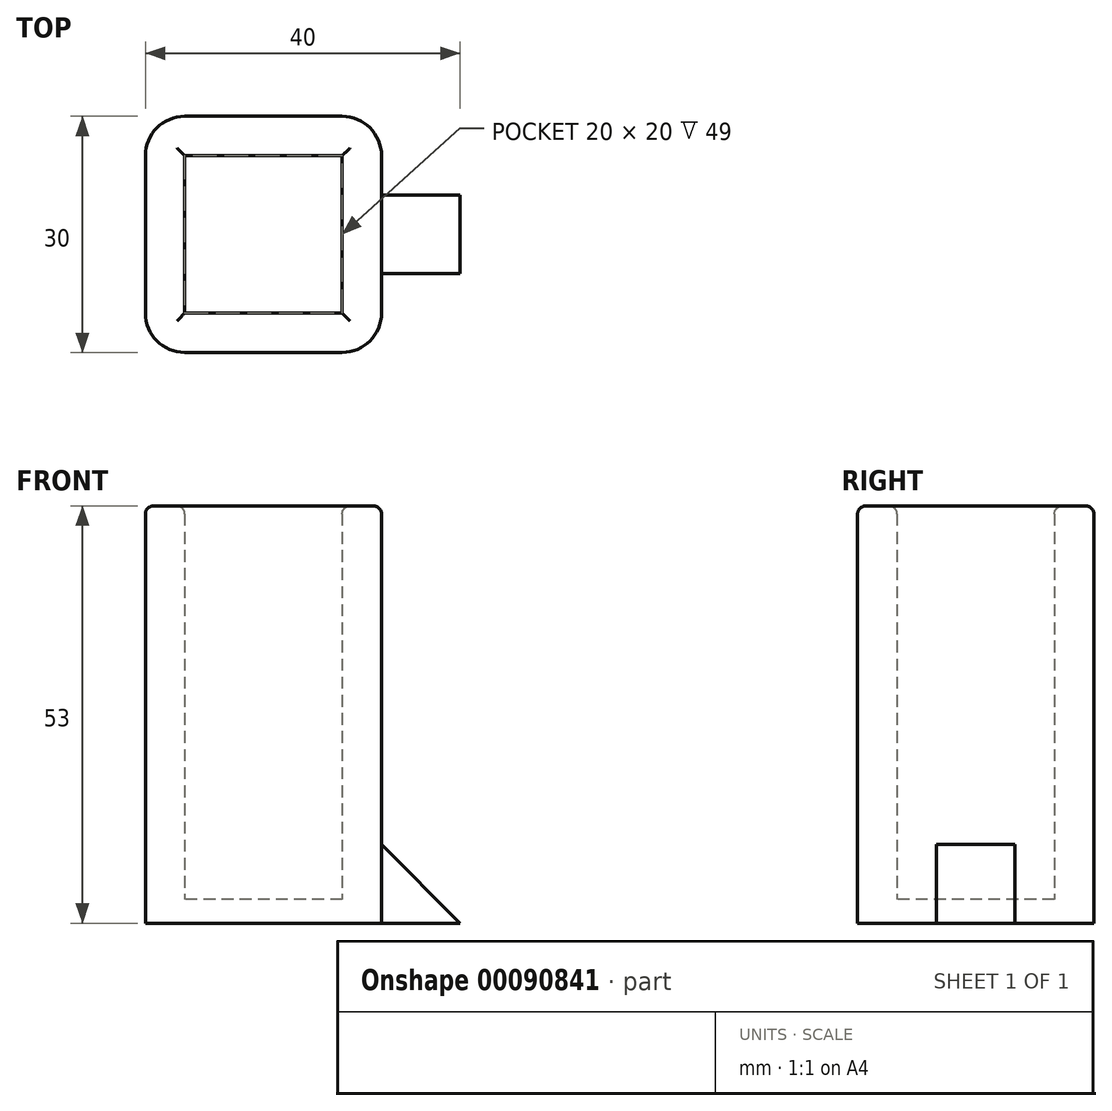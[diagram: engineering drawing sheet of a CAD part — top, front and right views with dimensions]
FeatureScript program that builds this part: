
annotation { "Feature Type Name" : "Feature", "Feature Type Description" : "" }
export const myFeature = defineFeature(function(context is Context, id is Id, definition is map)
    precondition{}
    {
        {
            var Q0;
            Q0=qCreatedBy(makeId("Top.planeOp"),FACE);
            var sketch = newSketch(context, id + "F0", { "sketchPlane" : qUnion([Q0])});
            skLineSegment(sketch, "E0.bottom", {"start": v(15, 15) * mm, "end": v(-15, 15) * mm});
            skLineSegment(sketch, "E0.top", {"start": v(15, -15) * mm, "end": v(-15, -15) * mm});
            skLineSegment(sketch, "E0.left", {"start": v(15, 15) * mm, "end": v(15, -15) * mm});
            skLineSegment(sketch, "E0.right", {"start": v(-15, 15) * mm, "end": v(-15, -15) * mm});
            skPoint(sketch, "E0.middle", {"position": v(0, 0) * mm});
            skSolve(sketch);
        }
        {
            var Q0;
            Q0 = qSketchRegion(id + "F0", true);
            extrude(context, id + "F1", {"entities" : qUnion([Q0]), "depth" : 3 * mm});
        }
        {
            var Q0;
            Q0=makeQuery(id+"F1.opExtrude","CAP_FACE",FACE,{"disambiguationData":[OSD([sQuery(id+"F0.wireOp",EDGE,"E0.bottom"),sQuery(id+"F0.wireOp",EDGE,"E0.top"),sQuery(id+"F0.wireOp",EDGE,"E0.left"),sQuery(id+"F0.wireOp",EDGE,"E0.right")])],"isStart":false});
            var sketch = newSketch(context, id + "F2", { "sketchPlane" : qUnion([Q0])});
            skLineSegment(sketch, "E1.bottom", {"start": v(15, 15) * mm, "end": v(-15, 15) * mm});
            skLineSegment(sketch, "E1.top", {"start": v(15, -15) * mm, "end": v(-15, -15) * mm});
            skLineSegment(sketch, "E1.left", {"start": v(15, 15) * mm, "end": v(15, -15) * mm});
            skLineSegment(sketch, "E1.right", {"start": v(-15, 15) * mm, "end": v(-15, -15) * mm});
            skPoint(sketch, "E1.middle", {"position": v(0, 0) * mm});
            skLineSegment(sketch, "E2.bottom", {"start": v(10, 10) * mm, "end": v(-10, 10) * mm});
            skLineSegment(sketch, "E2.top", {"start": v(10, -10) * mm, "end": v(-10, -10) * mm});
            skLineSegment(sketch, "E2.left", {"start": v(10, 10) * mm, "end": v(10, -10) * mm});
            skLineSegment(sketch, "E2.right", {"start": v(-10, 10) * mm, "end": v(-10, -10) * mm});
            skSolve(sketch);
        }
        {
            var Q0;
            Q0 = qSketchRegion(id + "F2", true);
            extrude(context, id + "F3", {"entities" : qUnion([Q0]), "operationType" : NewBodyOperationType.ADD, "depth" : 50 * mm});
        }
        {
            var Q0;
            Q0=makeQuery(id+"F3.boolean.opBoolean","MERGE",EDGE,{"derivedFrom":[makeQuery(id+"F1.opExtrude","SWEPT_EDGE",EDGE,{"disambiguationData":[OSD([sQuery(id+"F0.wireOp",EDGE,"E0.top"),sQuery(id+"F0.wireOp",EDGE,"E0.right")])]}),makeQuery(id+"F3.opExtrude","SWEPT_EDGE",EDGE,{"disambiguationData":[OSD([sQuery(id+"F2.wireOp",EDGE,"E1.top"),sQuery(id+"F2.wireOp",EDGE,"E1.right")])]})]});
            var Q1;
            Q1=makeQuery(id+"F3.boolean.opBoolean","MERGE",EDGE,{"derivedFrom":[makeQuery(id+"F1.opExtrude","SWEPT_EDGE",EDGE,{"disambiguationData":[OSD([sQuery(id+"F0.wireOp",EDGE,"E0.bottom"),sQuery(id+"F0.wireOp",EDGE,"E0.right")])]}),makeQuery(id+"F3.opExtrude","SWEPT_EDGE",EDGE,{"disambiguationData":[OSD([sQuery(id+"F2.wireOp",EDGE,"E1.bottom"),sQuery(id+"F2.wireOp",EDGE,"E1.right")])]})]});
            var Q2;
            Q2=makeQuery(id+"F3.boolean.opBoolean","MERGE",EDGE,{"derivedFrom":[makeQuery(id+"F1.opExtrude","SWEPT_EDGE",EDGE,{"disambiguationData":[OSD([sQuery(id+"F0.wireOp",EDGE,"E0.bottom"),sQuery(id+"F0.wireOp",EDGE,"E0.left")])]}),makeQuery(id+"F3.opExtrude","SWEPT_EDGE",EDGE,{"disambiguationData":[OSD([sQuery(id+"F2.wireOp",EDGE,"E1.bottom"),sQuery(id+"F2.wireOp",EDGE,"E1.left")])]})]});
            var Q3;
            Q3=makeQuery(id+"F3.boolean.opBoolean","MERGE",EDGE,{"derivedFrom":[makeQuery(id+"F1.opExtrude","SWEPT_EDGE",EDGE,{"disambiguationData":[OSD([sQuery(id+"F0.wireOp",EDGE,"E0.top"),sQuery(id+"F0.wireOp",EDGE,"E0.left")])]}),makeQuery(id+"F3.opExtrude","SWEPT_EDGE",EDGE,{"disambiguationData":[OSD([sQuery(id+"F2.wireOp",EDGE,"E1.top"),sQuery(id+"F2.wireOp",EDGE,"E1.left")])]})]});
            fillet(context, id + "F4", {"entities" : qUnion([Q0, Q1, Q2, Q3]), "radius" : 5 * mm, "tangentPropagation" : true, "allowEdgeOverflow" : false});
        }
        {
            var Q0;
            Q0=makeQuery(id+"F3.opExtrude","CAP_FACE",FACE,{"disambiguationData":[OSD([sQuery(id+"F2.wireOp",EDGE,"E1.bottom"),sQuery(id+"F2.wireOp",EDGE,"E1.top"),sQuery(id+"F2.wireOp",EDGE,"E1.left"),sQuery(id+"F2.wireOp",EDGE,"E1.right"),sQuery(id+"F2.wireOp",EDGE,"E2.bottom"),sQuery(id+"F2.wireOp",EDGE,"E2.top"),sQuery(id+"F2.wireOp",EDGE,"E2.left"),sQuery(id+"F2.wireOp",EDGE,"E2.right")])],"isStart":false});
            fillet(context, id + "F5", {"entities" : qUnion([Q0]), "radius" : 1 * mm, "tangentPropagation" : true, "allowEdgeOverflow" : false});
        }
        {
            var Q0;
            Q0=qCreatedBy(makeId("Front.planeOp"),FACE);
            var sketch = newSketch(context, id + "F6", { "sketchPlane" : qUnion([Q0])});
            skLineSegment(sketch, "E3", {"start": v(15, 0) * mm, "end": v(15, 10) * mm});
            skLineSegment(sketch, "E4", {"start": v(15, 10) * mm, "end": v(25, 0) * mm});
            skLineSegment(sketch, "E5", {"start": v(25, 0) * mm, "end": v(15, 0) * mm});
            skLineSegment(sketch, "E6", {"start": v(0, 0) * mm, "end": v(0, 15) * mm, "construction": true});
            skSolve(sketch);
        }
        {
            var Q0;
            Q0 = qSketchRegion(id + "F6", true);
            extrude(context, id + "F7", {"entities" : qUnion([Q0]), "operationType" : NewBodyOperationType.ADD, "depth" : 5 * mm, "hasSecondDirection" : true, "secondDirectionOppositeDirection" : true, "secondDirectionDepth" : 5 * mm});
        }
    });
